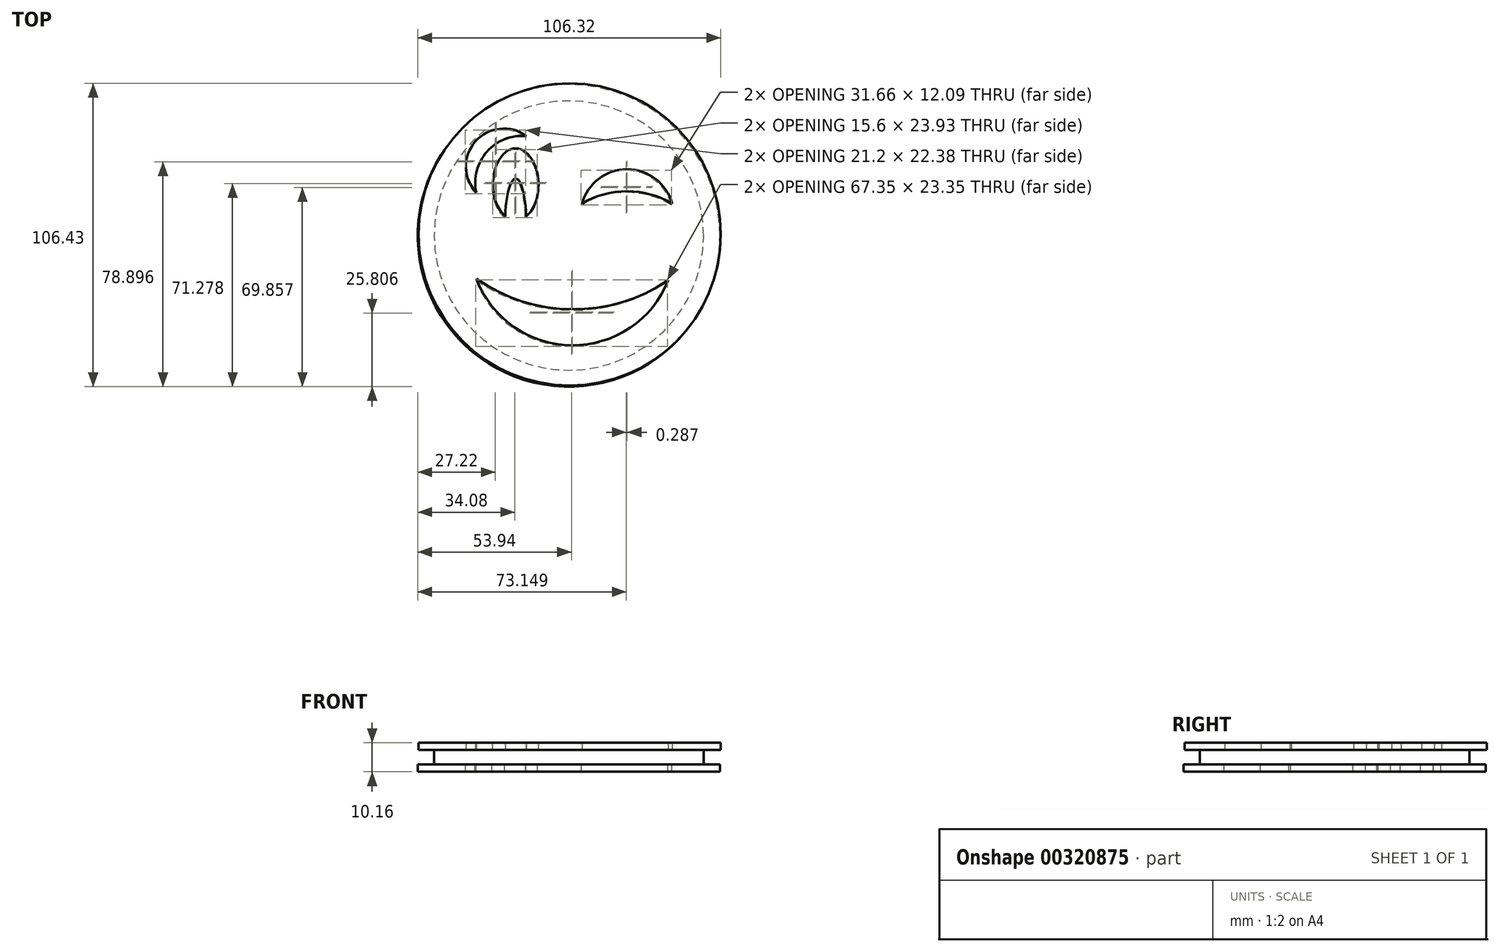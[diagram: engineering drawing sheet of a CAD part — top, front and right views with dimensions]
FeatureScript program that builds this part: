
annotation { "Feature Type Name" : "Feature", "Feature Type Description" : "" }
export const myFeature = defineFeature(function(context is Context, id is Id, definition is map)
    precondition{}
    {
        {
            var Q0;
            Q0=qCreatedBy(makeId("Top.planeOp"),FACE);
            var sketch = newSketch(context, id + "F0", { "sketchPlane" : qUnion([Q0])});
            skCircle(sketch, "E0", {"center": v(0, 0) * mm, "radius": 53.02 * mm});
            skPoint(sketch, "E1.start.orphan", {"position": v(-115.8, 39.35) * mm});
            skArc(sketch, "E2", {"start": v(35.96, 10.8) * mm, "mid": v(20.13, 22.88) * mm, "end": v(4.3, 10.8) * mm});
            skArc(sketch, "E3", {"start": v(35.96, 10.8) * mm, "mid": v(20.13, 15.17) * mm, "end": v(4.3, 10.8) * mm});
            skLineSegment(sketch, "E4", {"start": v(-13.77, 9.59) * mm, "end": v(-13.77, 9.59) * mm});
            skPoint(sketch, "E5.center.orphan", {"position": v(-10.6, 10.8) * mm});
            skEllipticalArc(sketch, "E6", {});
            skEllipticalArc(sketch, "E7", {});
            skArc(sketch, "E8", {"start": v(-15.2, 34.54) * mm, "mid": v(-33.07, 32.65) * mm, "end": v(-32.76, 14.68) * mm});
            skArc(sketch, "E9", {"start": v(-15.2, 34.54) * mm, "mid": v(-29.02, 29.07) * mm, "end": v(-32.76, 14.68) * mm});
            skArc(sketch, "E10", {"start": v(-32.76, -15.54) * mm, "mid": v(0.72, -38.89) * mm, "end": v(34.6, -16.12) * mm});
            skArc(sketch, "E11", {"start": v(-32.76, -15.54) * mm, "mid": v(0.83, -26.26) * mm, "end": v(34.6, -16.12) * mm});
            const initialGuessF0  = {"E6": [-0.018939891830086708, 0.017559814266860485, 0, -1, 0.012664157897233965, 0.00802599836855004, 0.474035322036162, 5.809149985143424], "E7": [-0.018939891830086708, 0.00489565636962652, 0, -1, 0.014679105021059511, 0.0036804019385780424, 1.666071027570438, 4.617114279609148]};
            skSetInitialGuess(sketch, initialGuessF0);
            skSolve(sketch);
        }
        {
            var Q0;
            Q0=makeQuery(id+"F0.imprint","IMPRINT",FACE,{"disambiguationData":[TD([[makeQuery(id+"F0.imprint","IMPRINT",EDGE,{"derivedFrom":sQuery(id+"F0.wireOp",EDGE,"E0")}),1.0]])]});
            extrude(context, id + "F1", {"entities" : qUnion([Q0]), "depth" : 2.54 * mm});
        }
        {
            var Q0;
            Q0=makeQuery(id+"F1.opExtrude","CAP_FACE",FACE,{"disambiguationData":[OSD([sQuery(id+"F0.wireOp",EDGE,"E0"),sQuery(id+"F0.wireOp",EDGE,"E2"),sQuery(id+"F0.wireOp",EDGE,"E3"),sQuery(id+"F0.wireOp",EDGE,"E6"),sQuery(id+"F0.wireOp",EDGE,"E7"),sQuery(id+"F0.wireOp",EDGE,"E8"),sQuery(id+"F0.wireOp",EDGE,"E9"),sQuery(id+"F0.wireOp",EDGE,"E10"),sQuery(id+"F0.wireOp",EDGE,"E11")])],"isStart":false});
            var sketch = newSketch(context, id + "F2", { "sketchPlane" : qUnion([Q0])});
            skCircle(sketch, "E12", {"center": v(0, 0) * mm, "radius": 47.26 * mm});
            skSolve(sketch);
        }
        {
            var Q0;
            Q0 = qSketchRegion(id + "F2", true);
            extrude(context, id + "F3", {"entities" : qUnion([Q0]), "depth" : 5.08 * mm});
        }
        {
            var Q0;
            Q0=makeQuery(id+"F3.opExtrude","CAP_FACE",FACE,{"disambiguationData":[OSD([sQuery(id+"F2.wireOp",EDGE,"E12")])],"isStart":false});
            var sketch = newSketch(context, id + "F4", { "sketchPlane" : qUnion([Q0])});
            skCircle(sketch, "E13", {"center": v(0.29, 0.4) * mm, "radius": 53.02 * mm});
            skPoint(sketch, "E14.start.orphan", {"position": v(-115.52, 39.75) * mm});
            skArc(sketch, "E15", {"start": v(36.25, 11.19) * mm, "mid": v(20.42, 23.28) * mm, "end": v(4.59, 11.19) * mm});
            skArc(sketch, "E16", {"start": v(36.25, 11.19) * mm, "mid": v(20.42, 15.57) * mm, "end": v(4.59, 11.19) * mm});
            skLineSegment(sketch, "E17", {"start": v(-36.6, -16.18) * mm, "end": v(-36.6, -16.18) * mm});
            skPoint(sketch, "E18.center.orphan", {"position": v(-10.32, 11.19) * mm});
            skEllipticalArc(sketch, "E19", {});
            skEllipticalArc(sketch, "E20", {});
            skArc(sketch, "E21", {"start": v(-14.91, 34.94) * mm, "mid": v(-32.78, 33.05) * mm, "end": v(-32.47, 15.08) * mm});
            skArc(sketch, "E22", {"start": v(-14.91, 34.94) * mm, "mid": v(-28.73, 29.47) * mm, "end": v(-32.47, 15.08) * mm});
            skArc(sketch, "E23", {"start": v(-32.47, -15.14) * mm, "mid": v(1, -38.5) * mm, "end": v(34.88, -15.73) * mm});
            skArc(sketch, "E24", {"start": v(-32.47, -15.14) * mm, "mid": v(1.12, -25.86) * mm, "end": v(34.88, -15.73) * mm});
            const initialGuessF4  = {"E19": [-0.018652619794011116, 0.017958779473720668, 0, -1, 0.012664157897233965, 0.00802599836855004, 0.4740353220361621, 5.809149985143424], "E20": [-0.018652619794011116, 0.005294621576486705, 0, -1, 0.014679105021059511, 0.0036804019385780424, 1.666071027570438, 4.617114279609148]};
            skSetInitialGuess(sketch, initialGuessF4);
            skSolve(sketch);
        }
        {
            var Q0;
            Q0 = qSketchRegion(id + "F4", true);
            extrude(context, id + "F5", {"entities" : qUnion([Q0]), "depth" : 2.54 * mm});
        }
    });
